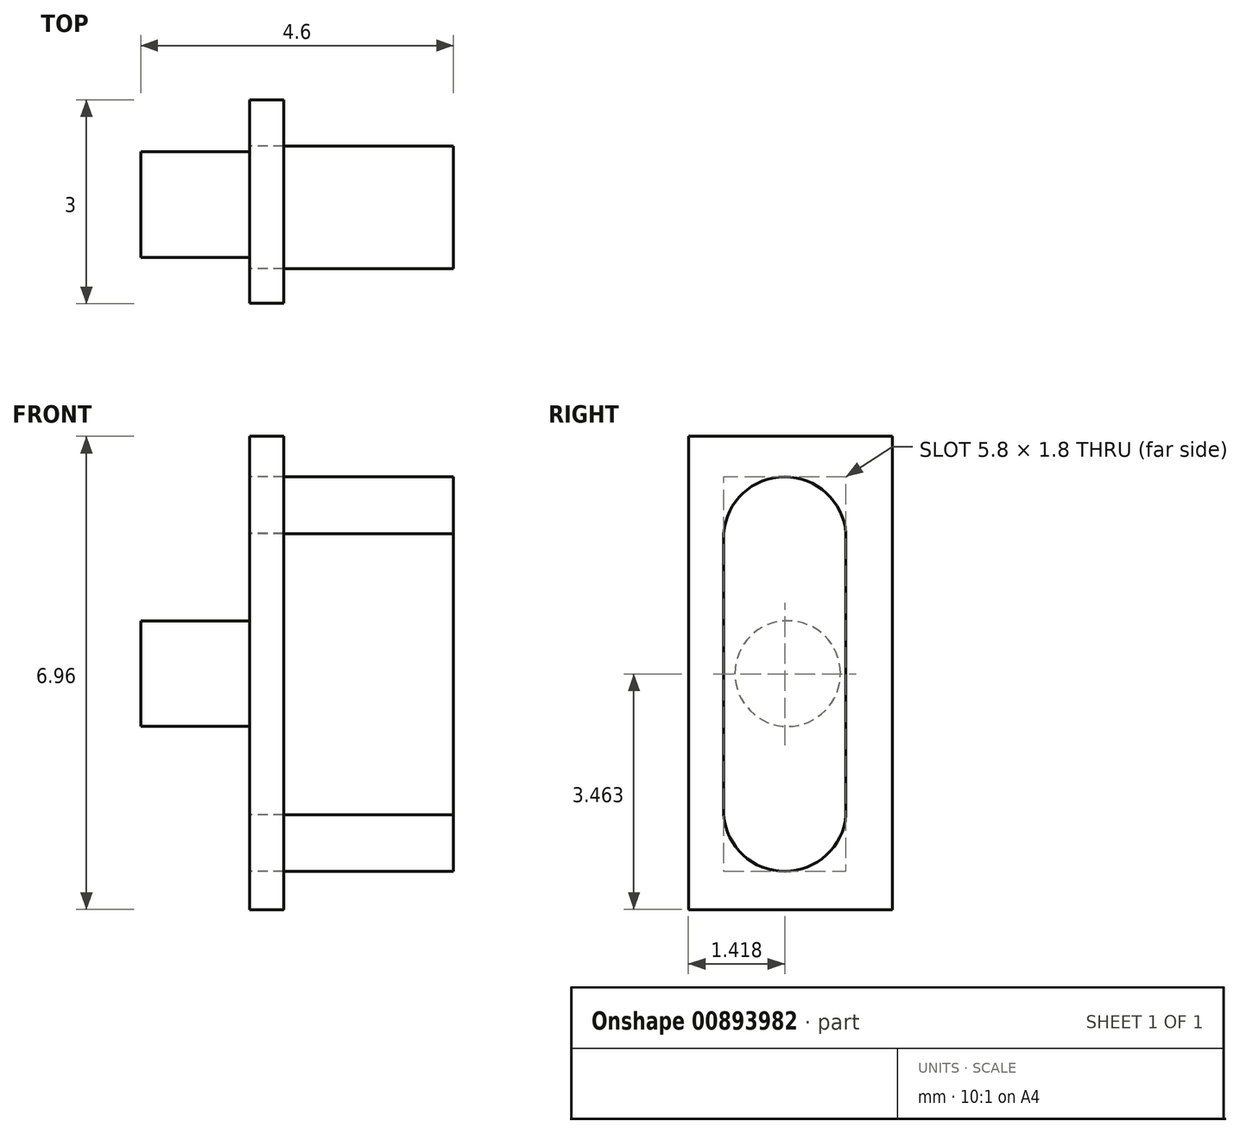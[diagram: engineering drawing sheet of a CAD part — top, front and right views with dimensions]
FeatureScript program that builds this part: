
annotation { "Feature Type Name" : "Feature", "Feature Type Description" : "" }
export const myFeature = defineFeature(function(context is Context, id is Id, definition is map)
    precondition{}
    {
        {
            var Q0;
            Q0=qCreatedBy(makeId("Right.planeOp"),FACE);
            var sketch = newSketch(context, id + "F0", { "sketchPlane" : qUnion([Q0])});
            skLineSegment(sketch, "E0.bottom", {"start": v(-1.46, -3.47) * mm, "end": v(1.54, -3.47) * mm});
            skLineSegment(sketch, "E0.top", {"start": v(-1.46, 3.5) * mm, "end": v(1.54, 3.5) * mm});
            skLineSegment(sketch, "E0.left", {"start": v(-1.46, -3.47) * mm, "end": v(-1.46, 3.5) * mm});
            skLineSegment(sketch, "E0.right", {"start": v(1.54, -3.47) * mm, "end": v(1.54, 3.5) * mm});
            skLineSegment(sketch, "E1", {"start": v(-0.94, 2.06) * mm, "end": v(-0.94, -2.08) * mm});
            skArc(sketch, "E2", {"start": v(-0.94, -2.08) * mm, "mid": v(-0.04, -2.9) * mm, "end": v(0.86, -2.08) * mm});
            skLineSegment(sketch, "E3", {"start": v(0.86, -2.08) * mm, "end": v(0.86, 2.06) * mm});
            skArc(sketch, "E4", {"start": v(0.86, 2.06) * mm, "mid": v(-0.04, 2.9) * mm, "end": v(-0.94, 2.06) * mm});
            skSolve(sketch);
        }
        {
            var Q0;
            Q0 = qSketchRegion(id + "F0", true);
            extrude(context, id + "F1", {"entities" : qUnion([Q0]), "depth" : 0.5 * mm, "offsetDistance" : 25 * mm});
        }
        {
            var Q0;
            Q0=makeQuery(id+"F0.imprint","IMPRINT",FACE,{"disambiguationData":[TD([[makeQuery(id+"F0.imprint","IMPRINT",EDGE,{"derivedFrom":sQuery(id+"F0.wireOp",EDGE,"E1")}),1.0]])]});
            extrude(context, id + "F2", {"entities" : qUnion([Q0]), "depth" : 3 * mm, "offsetDistance" : 25 * mm});
        }
        {
            var Q0;
            Q0=makeQuery(id+"F2.opExtrude","CAP_FACE",FACE,{"disambiguationData":[OSD([sQuery(id+"F0.wireOp",EDGE,"E1"),sQuery(id+"F0.wireOp",EDGE,"E2"),sQuery(id+"F0.wireOp",EDGE,"E3"),sQuery(id+"F0.wireOp",EDGE,"E4")])],"isStart":true});
            var sketch = newSketch(context, id + "F3", { "sketchPlane" : qUnion([Q0])});
            skCircle(sketch, "E5", {"center": v(0, 0) * mm, "radius": 0.78 * mm});
            skSolve(sketch);
        }
        {
            var Q0;
            Q0=makeQuery(id+"F3.imprint","IMPRINT",FACE,{"disambiguationData":[TD([[makeQuery(id+"F3.imprint","IMPRINT",EDGE,{"derivedFrom":sQuery(id+"F3.wireOp",EDGE,"E5")}),1.0]])]});
            extrude(context, id + "F4", {"entities" : qUnion([Q0]), "operationType" : NewBodyOperationType.ADD, "depth" : 1.6 * mm, "offsetDistance" : 25 * mm});
        }
    });
